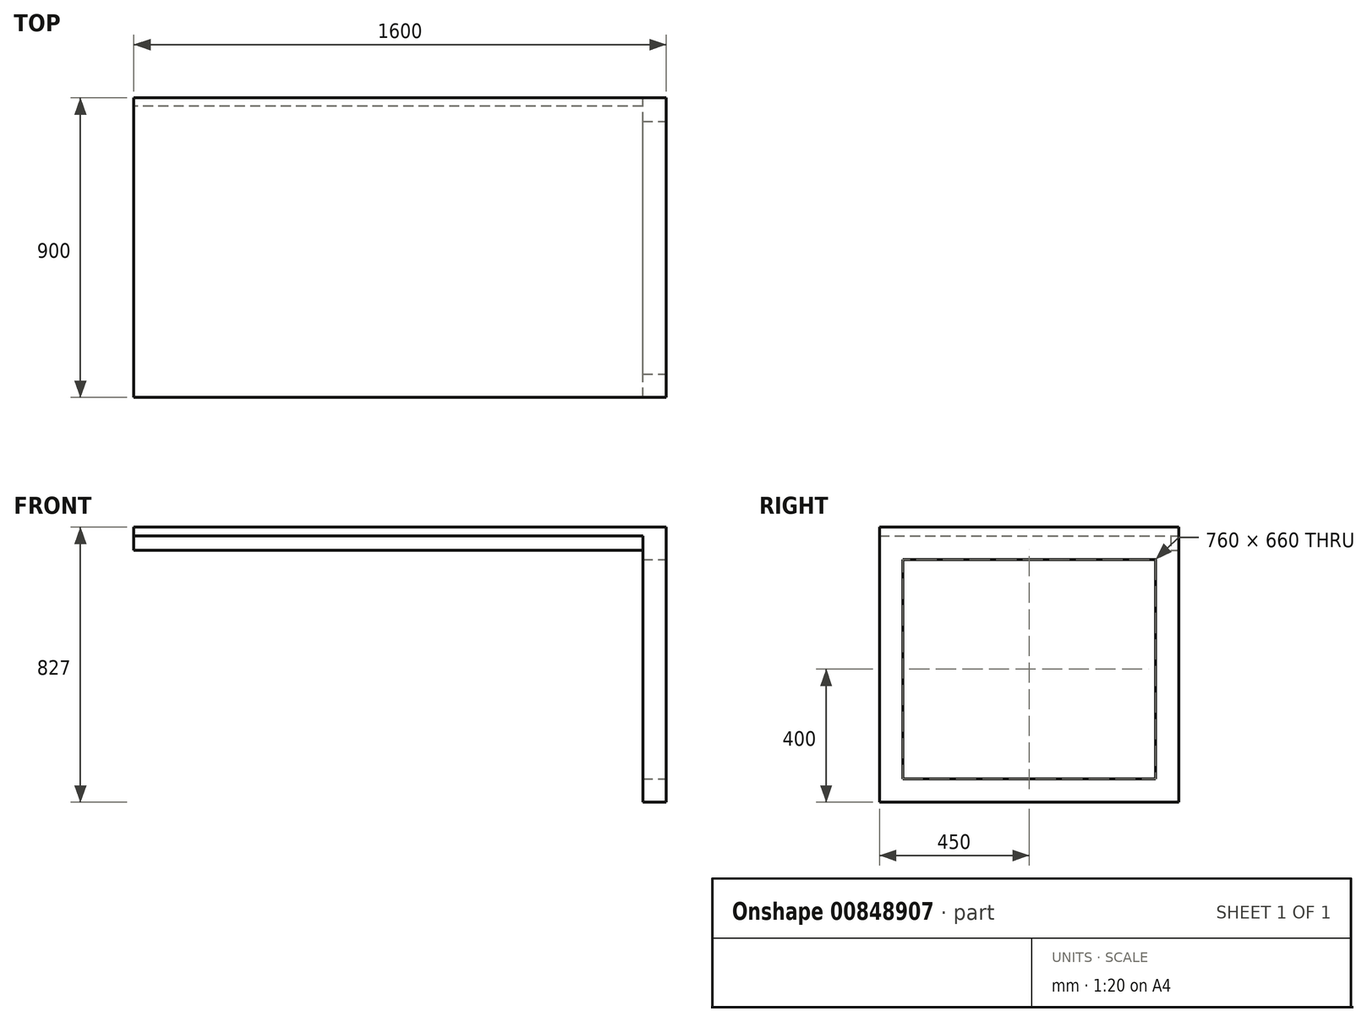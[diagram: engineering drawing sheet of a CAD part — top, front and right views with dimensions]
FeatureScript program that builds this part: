
annotation { "Feature Type Name" : "Feature", "Feature Type Description" : "" }
export const myFeature = defineFeature(function(context is Context, id is Id, definition is map)
    precondition{}
    {
        {
            var Q0;
            Q0=qCreatedBy(makeId("Top.planeOp"),FACE);
            var sketch = newSketch(context, id + "F0", { "sketchPlane" : qUnion([Q0])});
            skLineSegment(sketch, "E0.bottom", {"start": v(-800, -450) * mm, "end": v(800, -450) * mm});
            skLineSegment(sketch, "E0.top", {"start": v(-800, 450) * mm, "end": v(800, 450) * mm});
            skLineSegment(sketch, "E0.left", {"start": v(-800, -450) * mm, "end": v(-800, 450) * mm});
            skLineSegment(sketch, "E0.right", {"start": v(800, -450) * mm, "end": v(800, 450) * mm});
            skPoint(sketch, "E0.middle", {"position": v(0, 0) * mm});
            skSolve(sketch);
        }
        {
            var Q0;
            Q0 = qSketchRegion(id + "F0", true);
            extrude(context, id + "F1", {"entities" : qUnion([Q0]), "depth" : 27 * mm, "offsetDistance" : 25 * mm});
        }
        {
            var Q0;
            Q0=makeQuery(id+"F1.opExtrude","SWEPT_FACE",FACE,{"disambiguationData":[OSD([sQuery(id+"F0.wireOp",EDGE,"E0.right")])]});
            var sketch = newSketch(context, id + "F2", { "sketchPlane" : qUnion([Q0])});
            skLineSegment(sketch, "E1.bottom", {"start": v(-450, 0) * mm, "end": v(450, 0) * mm});
            skLineSegment(sketch, "E1.top", {"start": v(-450, -800) * mm, "end": v(450, -800) * mm});
            skLineSegment(sketch, "E1.left", {"start": v(-450, 0) * mm, "end": v(-450, -800) * mm});
            skLineSegment(sketch, "E1.right", {"start": v(450, 0) * mm, "end": v(450, -800) * mm});
            skLineSegment(sketch, "E2.0", {"start": v(-380, -70) * mm, "end": v(-380, -730) * mm});
            skLineSegment(sketch, "E2.1", {"start": v(-380, -70) * mm, "end": v(380, -70) * mm});
            skLineSegment(sketch, "E2.2", {"start": v(380, -70) * mm, "end": v(380, -730) * mm});
            skLineSegment(sketch, "E2.3", {"start": v(-380, -730) * mm, "end": v(380, -730) * mm});
            skSolve(sketch);
        }
        {
            var Q0;
            Q0=makeQuery(id+"F2.imprint","IMPRINT",FACE,{"disambiguationData":[TD([[makeQuery(id+"F2.imprint","IMPRINT",EDGE,{"derivedFrom":sQuery(id+"F2.wireOp",EDGE,"E1.bottom")}),-1.0]])]});
            extrude(context, id + "F3", {"entities" : qUnion([Q0]), "operationType" : NewBodyOperationType.ADD, "oppositeDirection" : true, "depth" : 70 * mm, "offsetDistance" : 25 * mm});
        }
        {
            var Q0;
            {var subQ0=sQuery(id+"F2.wireOp",EDGE,"E1.right");Q0=makeQuery(id+"FNJFjf2BKvGuvSB_1.1.F3.boolean.opBoolean","MERGE",FACE,{"derivedFrom":[makeQuery(id+"F3.boolean.opBoolean","MERGE",FACE,{"derivedFrom":[makeQuery(id+"F1.opExtrude","SWEPT_FACE",FACE,{"disambiguationData":[OSD([sQuery(id+"F0.wireOp",EDGE,"E0.top")])]}),makeQuery(id+"F3.opExtrude","SWEPT_FACE",FACE,{"disambiguationData":[OSD([subQ0])]})]}),makeQuery(id+"FNJFjf2BKvGuvSB_1.1.F3.opExtrude","SWEPT_FACE",FACE,{"disambiguationData":[OSD([subQ0])]})]});}
            var sketch = newSketch(context, id + "F4", { "sketchPlane" : qUnion([Q0])});
            skLineSegment(sketch, "E3.bottom", {"start": v(-800, 27) * mm, "end": v(800, 27) * mm});
            skLineSegment(sketch, "E3.top", {"start": v(-800, -43) * mm, "end": v(800, -43) * mm});
            skLineSegment(sketch, "E3.left", {"start": v(-800, 27) * mm, "end": v(-800, -43) * mm});
            skLineSegment(sketch, "E3.right", {"start": v(800, 27) * mm, "end": v(800, -43) * mm});
            skSolve(sketch);
        }
        {
            var Q0;
            {var subQ6=makeQuery(id+"F1.opExtrude","CAP_EDGE",EDGE,{"disambiguationData":[OSD([sQuery(id+"F0.wireOp",EDGE,"E0.top")])],"isStart":true});Q0=makeQuery(id+"F4.imprint","IMPRINT",FACE,{"disambiguationData":[TD([[makeQuery(id+"F4.imprint","IMPRINT",EDGE,{"derivedFrom":subQ6}),1.0]])]});}
            extrude(context, id + "F5", {"entities" : qUnion([Q0]), "oppositeDirection" : true, "depth" : 25 * mm, "offsetDistance" : 25 * mm});
        }
    });
